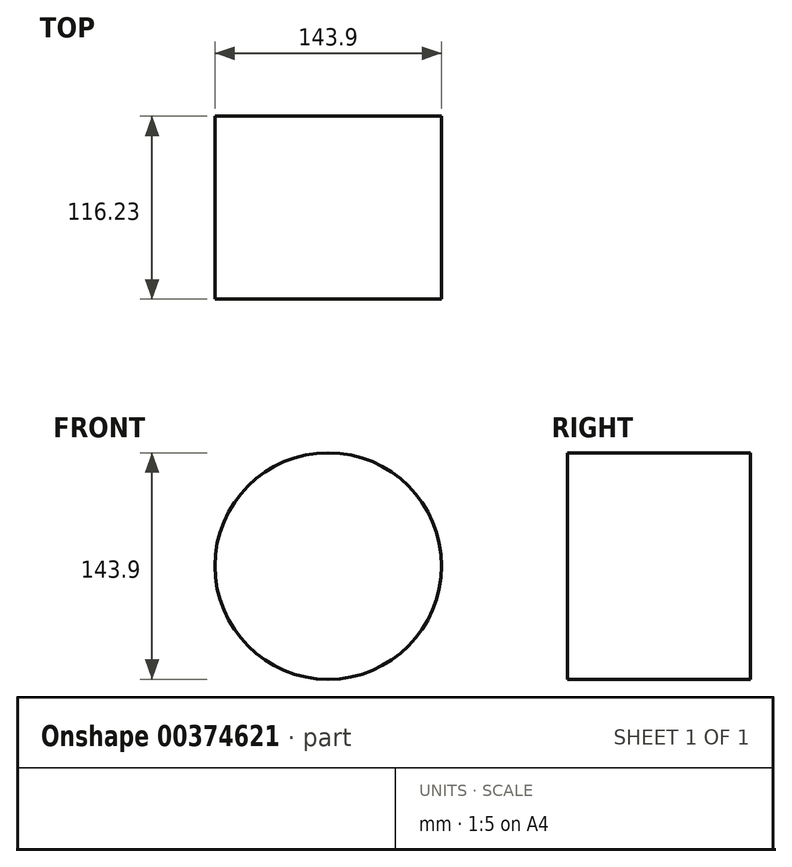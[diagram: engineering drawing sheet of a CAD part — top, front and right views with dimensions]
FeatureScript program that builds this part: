
annotation { "Feature Type Name" : "Feature", "Feature Type Description" : "" }
export const myFeature = defineFeature(function(context is Context, id is Id, definition is map)
    precondition{}
    {
        {
            var Q0;
            Q0=qCreatedBy(makeId("Front.planeOp"),FACE);
            var sketch = newSketch(context, id + "F0", { "sketchPlane" : qUnion([Q0])});
            skCircle(sketch, "E0", {"center": v(0, 0) * mm, "radius": 71.95 * mm});
            skSolve(sketch);
        }
        {
            var Q0;
            Q0=makeQuery(id+"F0.imprint","IMPRINT",FACE,{"disambiguationData":[TD([[makeQuery(id+"F0.imprint","IMPRINT",EDGE,{"derivedFrom":sQuery(id+"F0.wireOp",EDGE,"E0")}),1.0]])]});
            extrude(context, id + "F1", {"entities" : qUnion([Q0]), "depth" : 116.23 * mm});
        }
    });
